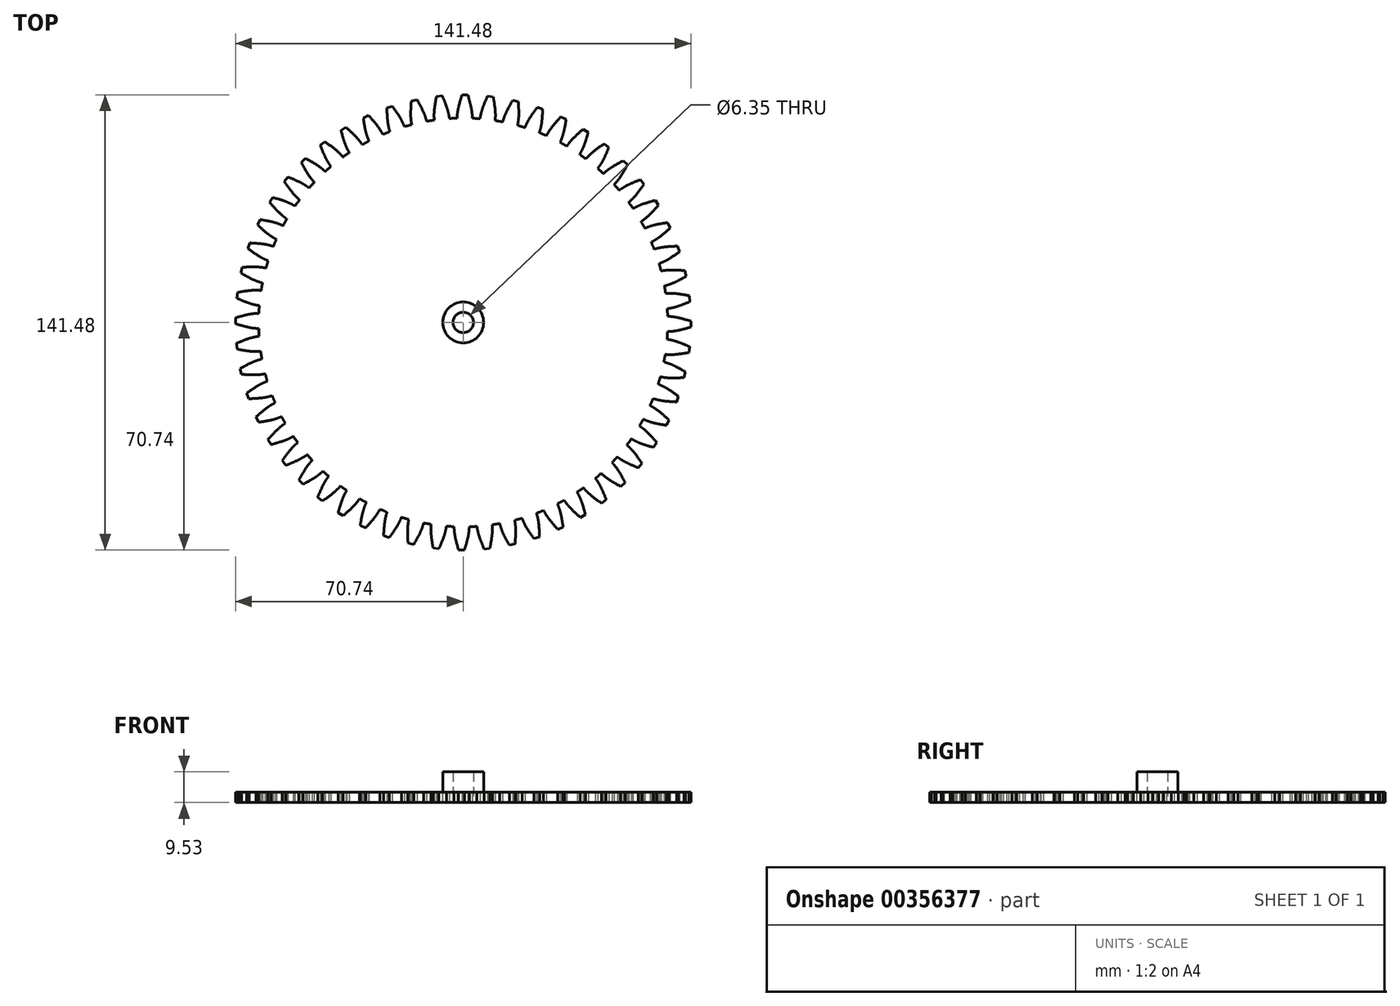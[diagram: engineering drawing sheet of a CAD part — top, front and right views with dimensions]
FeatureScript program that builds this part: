
annotation { "Feature Type Name" : "Feature", "Feature Type Description" : "" }
export const myFeature = defineFeature(function(context is Context, id is Id, definition is map)
    precondition{}
    {
        {
            var Q0;
            Q0=qCreatedBy(makeId("Top.planeOp"),FACE);
            var sketch = newSketch(context, id + "F0", { "sketchPlane" : qUnion([Q0])});
            skLineSegment(sketch, "E0.14", {"start": v(5.82, 65.97) * mm, "end": v(9.98, 65.46) * mm});
            skLineSegment(sketch, "E1.14", {"start": v(5.22, 63.33) * mm, "end": v(9.94, 62.76) * mm});
            skLineSegment(sketch, "E2", {"start": v(0, 0) * mm, "end": v(8.44, 70.23) * mm});
            skLineSegment(sketch, "E3", {"start": v(7.53, 70.34) * mm, "end": v(9.35, 70.12) * mm});
            skPoint(sketch, "E4", {"position": v(7.58, 63.05) * mm});
            skPoint(sketch, "E5", {"position": v(7.9, 65.72) * mm});
            skPoint(sketch, "E6", {"position": v(8.44, 70.23) * mm});
            skFitSpline(sketch, "E7", {"points": [v(5.22, 63.33) * mm, v(5.82, 65.97) * mm, v(7.53, 70.34) * mm], "startDerivative": vector(1.04, 5.77) * mm, "endDerivative": vector(3.48, 8.14) * mm});
            skFitSpline(sketch, "E8", {"points": [v(9.35, 70.12) * mm, v(9.98, 65.46) * mm, v(9.94, 62.76) * mm], "startDerivative": vector(1.45, -8.73) * mm, "endDerivative": vector(-0.36, -5.85) * mm});
            skCircle(sketch, "E9", {"center": v(0, 0) * mm, "radius": 63.54 * mm});
            skSolve(sketch);
        }
        {
            var Q0;
            Q0 = qSketchRegion(id + "F0", true);
            extrude(context, id + "F1", {"entities" : qUnion([Q0]), "depth" : 3.17 * mm, "offsetDistance" : 25.4 * mm});
        }
        {
            var Q0;
            Q0=qCreatedBy(makeId("Front.planeOp"),FACE);
            var sketch = newSketch(context, id + "F2", { "sketchPlane" : qUnion([Q0])});
            skLineSegment(sketch, "E10", {"start": v(0, 0) * mm, "end": v(0, 55.23) * mm});
            skSolve(sketch);
        }
        {
            var Q0;
            Q0=makeQuery(id+"F1.opExtrude","SWEPT_BODY",BODY,{"disambiguationData":[OSD([sQuery(id+"F0.wireOp",EDGE,"E3"),sQuery(id+"F0.wireOp",EDGE,"E7"),sQuery(id+"F0.wireOp",EDGE,"E8"),sQuery(id+"F0.wireOp",EDGE,"E9")])]});
            var Q1;
            Q1=sQuery(id+"F2.wireOp",EDGE,"E10");
            circularPattern(context, id + "F3", {"entities" : qUnion([Q0]), "axis" : qUnion([Q1]), "angle" : 360 * degree, "instanceCount" : 56, "equalSpace" : true});
        }
        {
            var Q0;
            Q0=makeQuery(id+"F3.opPattern","COPY",BODY,{"derivedFrom":makeQuery(id+"F1.opExtrude","SWEPT_BODY",BODY,{"disambiguationData":[OSD([sQuery(id+"F0.wireOp",EDGE,"E3"),sQuery(id+"F0.wireOp",EDGE,"E7"),sQuery(id+"F0.wireOp",EDGE,"E8"),sQuery(id+"F0.wireOp",EDGE,"E9")])]}),"instanceName":"55"});
            var Q1;
            Q1=makeQuery(id+"F3.opPattern","COPY",BODY,{"derivedFrom":makeQuery(id+"F1.opExtrude","SWEPT_BODY",BODY,{"disambiguationData":[OSD([sQuery(id+"F0.wireOp",EDGE,"E3"),sQuery(id+"F0.wireOp",EDGE,"E7"),sQuery(id+"F0.wireOp",EDGE,"E8"),sQuery(id+"F0.wireOp",EDGE,"E9")])]}),"instanceName":"6"});
            var Q2;
            Q2=makeQuery(id+"F3.opPattern","COPY",BODY,{"derivedFrom":makeQuery(id+"F1.opExtrude","SWEPT_BODY",BODY,{"disambiguationData":[OSD([sQuery(id+"F0.wireOp",EDGE,"E3"),sQuery(id+"F0.wireOp",EDGE,"E7"),sQuery(id+"F0.wireOp",EDGE,"E8"),sQuery(id+"F0.wireOp",EDGE,"E9")])]}),"instanceName":"11"});
            var Q3;
            Q3=makeQuery(id+"F3.opPattern","COPY",BODY,{"derivedFrom":makeQuery(id+"F1.opExtrude","SWEPT_BODY",BODY,{"disambiguationData":[OSD([sQuery(id+"F0.wireOp",EDGE,"E3"),sQuery(id+"F0.wireOp",EDGE,"E7"),sQuery(id+"F0.wireOp",EDGE,"E8"),sQuery(id+"F0.wireOp",EDGE,"E9")])]}),"instanceName":"30"});
            var Q4;
            Q4=makeQuery(id+"F3.opPattern","COPY",BODY,{"derivedFrom":makeQuery(id+"F1.opExtrude","SWEPT_BODY",BODY,{"disambiguationData":[OSD([sQuery(id+"F0.wireOp",EDGE,"E3"),sQuery(id+"F0.wireOp",EDGE,"E7"),sQuery(id+"F0.wireOp",EDGE,"E8"),sQuery(id+"F0.wireOp",EDGE,"E9")])]}),"instanceName":"24"});
            var Q5;
            Q5=makeQuery(id+"F3.opPattern","COPY",BODY,{"derivedFrom":makeQuery(id+"F1.opExtrude","SWEPT_BODY",BODY,{"disambiguationData":[OSD([sQuery(id+"F0.wireOp",EDGE,"E3"),sQuery(id+"F0.wireOp",EDGE,"E7"),sQuery(id+"F0.wireOp",EDGE,"E8"),sQuery(id+"F0.wireOp",EDGE,"E9")])]}),"instanceName":"44"});
            var Q6;
            Q6=makeQuery(id+"F3.opPattern","COPY",BODY,{"derivedFrom":makeQuery(id+"F1.opExtrude","SWEPT_BODY",BODY,{"disambiguationData":[OSD([sQuery(id+"F0.wireOp",EDGE,"E3"),sQuery(id+"F0.wireOp",EDGE,"E7"),sQuery(id+"F0.wireOp",EDGE,"E8"),sQuery(id+"F0.wireOp",EDGE,"E9")])]}),"instanceName":"8"});
            var Q7;
            Q7=makeQuery(id+"F3.opPattern","COPY",BODY,{"derivedFrom":makeQuery(id+"F1.opExtrude","SWEPT_BODY",BODY,{"disambiguationData":[OSD([sQuery(id+"F0.wireOp",EDGE,"E3"),sQuery(id+"F0.wireOp",EDGE,"E7"),sQuery(id+"F0.wireOp",EDGE,"E8"),sQuery(id+"F0.wireOp",EDGE,"E9")])]}),"instanceName":"39"});
            var Q8;
            Q8=makeQuery(id+"F3.opPattern","COPY",BODY,{"derivedFrom":makeQuery(id+"F1.opExtrude","SWEPT_BODY",BODY,{"disambiguationData":[OSD([sQuery(id+"F0.wireOp",EDGE,"E3"),sQuery(id+"F0.wireOp",EDGE,"E7"),sQuery(id+"F0.wireOp",EDGE,"E8"),sQuery(id+"F0.wireOp",EDGE,"E9")])]}),"instanceName":"42"});
            var Q9;
            Q9=makeQuery(id+"F3.opPattern","COPY",BODY,{"derivedFrom":makeQuery(id+"F1.opExtrude","SWEPT_BODY",BODY,{"disambiguationData":[OSD([sQuery(id+"F0.wireOp",EDGE,"E3"),sQuery(id+"F0.wireOp",EDGE,"E7"),sQuery(id+"F0.wireOp",EDGE,"E8"),sQuery(id+"F0.wireOp",EDGE,"E9")])]}),"instanceName":"5"});
            var Q10;
            Q10=makeQuery(id+"F3.opPattern","COPY",BODY,{"derivedFrom":makeQuery(id+"F1.opExtrude","SWEPT_BODY",BODY,{"disambiguationData":[OSD([sQuery(id+"F0.wireOp",EDGE,"E3"),sQuery(id+"F0.wireOp",EDGE,"E7"),sQuery(id+"F0.wireOp",EDGE,"E8"),sQuery(id+"F0.wireOp",EDGE,"E9")])]}),"instanceName":"26"});
            var Q11;
            Q11=makeQuery(id+"F3.opPattern","COPY",BODY,{"derivedFrom":makeQuery(id+"F1.opExtrude","SWEPT_BODY",BODY,{"disambiguationData":[OSD([sQuery(id+"F0.wireOp",EDGE,"E3"),sQuery(id+"F0.wireOp",EDGE,"E7"),sQuery(id+"F0.wireOp",EDGE,"E8"),sQuery(id+"F0.wireOp",EDGE,"E9")])]}),"instanceName":"41"});
            var Q12;
            Q12=makeQuery(id+"F3.opPattern","COPY",BODY,{"derivedFrom":makeQuery(id+"F1.opExtrude","SWEPT_BODY",BODY,{"disambiguationData":[OSD([sQuery(id+"F0.wireOp",EDGE,"E3"),sQuery(id+"F0.wireOp",EDGE,"E7"),sQuery(id+"F0.wireOp",EDGE,"E8"),sQuery(id+"F0.wireOp",EDGE,"E9")])]}),"instanceName":"20"});
            var Q13;
            Q13=makeQuery(id+"F3.opPattern","COPY",BODY,{"derivedFrom":makeQuery(id+"F1.opExtrude","SWEPT_BODY",BODY,{"disambiguationData":[OSD([sQuery(id+"F0.wireOp",EDGE,"E3"),sQuery(id+"F0.wireOp",EDGE,"E7"),sQuery(id+"F0.wireOp",EDGE,"E8"),sQuery(id+"F0.wireOp",EDGE,"E9")])]}),"instanceName":"59"});
            var Q14;
            Q14=makeQuery(id+"F3.opPattern","COPY",BODY,{"derivedFrom":makeQuery(id+"F1.opExtrude","SWEPT_BODY",BODY,{"disambiguationData":[OSD([sQuery(id+"F0.wireOp",EDGE,"E3"),sQuery(id+"F0.wireOp",EDGE,"E7"),sQuery(id+"F0.wireOp",EDGE,"E8"),sQuery(id+"F0.wireOp",EDGE,"E9")])]}),"instanceName":"29"});
            var Q15;
            Q15=makeQuery(id+"F3.opPattern","COPY",BODY,{"derivedFrom":makeQuery(id+"F1.opExtrude","SWEPT_BODY",BODY,{"disambiguationData":[OSD([sQuery(id+"F0.wireOp",EDGE,"E3"),sQuery(id+"F0.wireOp",EDGE,"E7"),sQuery(id+"F0.wireOp",EDGE,"E8"),sQuery(id+"F0.wireOp",EDGE,"E9")])]}),"instanceName":"35"});
            var Q16;
            Q16=makeQuery(id+"F3.opPattern","COPY",BODY,{"derivedFrom":makeQuery(id+"F1.opExtrude","SWEPT_BODY",BODY,{"disambiguationData":[OSD([sQuery(id+"F0.wireOp",EDGE,"E3"),sQuery(id+"F0.wireOp",EDGE,"E7"),sQuery(id+"F0.wireOp",EDGE,"E8"),sQuery(id+"F0.wireOp",EDGE,"E9")])]}),"instanceName":"54"});
            var Q17;
            Q17=makeQuery(id+"F3.opPattern","COPY",BODY,{"derivedFrom":makeQuery(id+"F1.opExtrude","SWEPT_BODY",BODY,{"disambiguationData":[OSD([sQuery(id+"F0.wireOp",EDGE,"E3"),sQuery(id+"F0.wireOp",EDGE,"E7"),sQuery(id+"F0.wireOp",EDGE,"E8"),sQuery(id+"F0.wireOp",EDGE,"E9")])]}),"instanceName":"48"});
            var Q18;
            Q18=makeQuery(id+"F3.opPattern","COPY",BODY,{"derivedFrom":makeQuery(id+"F1.opExtrude","SWEPT_BODY",BODY,{"disambiguationData":[OSD([sQuery(id+"F0.wireOp",EDGE,"E3"),sQuery(id+"F0.wireOp",EDGE,"E7"),sQuery(id+"F0.wireOp",EDGE,"E8"),sQuery(id+"F0.wireOp",EDGE,"E9")])]}),"instanceName":"14"});
            var Q19;
            Q19=makeQuery(id+"F3.opPattern","COPY",BODY,{"derivedFrom":makeQuery(id+"F1.opExtrude","SWEPT_BODY",BODY,{"disambiguationData":[OSD([sQuery(id+"F0.wireOp",EDGE,"E3"),sQuery(id+"F0.wireOp",EDGE,"E7"),sQuery(id+"F0.wireOp",EDGE,"E8"),sQuery(id+"F0.wireOp",EDGE,"E9")])]}),"instanceName":"56"});
            var Q20;
            Q20=makeQuery(id+"F3.opPattern","COPY",BODY,{"derivedFrom":makeQuery(id+"F1.opExtrude","SWEPT_BODY",BODY,{"disambiguationData":[OSD([sQuery(id+"F0.wireOp",EDGE,"E3"),sQuery(id+"F0.wireOp",EDGE,"E7"),sQuery(id+"F0.wireOp",EDGE,"E8"),sQuery(id+"F0.wireOp",EDGE,"E9")])]}),"instanceName":"12"});
            var Q21;
            Q21=makeQuery(id+"F1.opExtrude","SWEPT_BODY",BODY,{"disambiguationData":[OSD([sQuery(id+"F0.wireOp",EDGE,"E3"),sQuery(id+"F0.wireOp",EDGE,"E7"),sQuery(id+"F0.wireOp",EDGE,"E8"),sQuery(id+"F0.wireOp",EDGE,"E9")])]});
            var Q22;
            Q22=makeQuery(id+"F3.opPattern","COPY",BODY,{"derivedFrom":makeQuery(id+"F1.opExtrude","SWEPT_BODY",BODY,{"disambiguationData":[OSD([sQuery(id+"F0.wireOp",EDGE,"E3"),sQuery(id+"F0.wireOp",EDGE,"E7"),sQuery(id+"F0.wireOp",EDGE,"E8"),sQuery(id+"F0.wireOp",EDGE,"E9")])]}),"instanceName":"49"});
            var Q23;
            Q23=makeQuery(id+"F3.opPattern","COPY",BODY,{"derivedFrom":makeQuery(id+"F1.opExtrude","SWEPT_BODY",BODY,{"disambiguationData":[OSD([sQuery(id+"F0.wireOp",EDGE,"E3"),sQuery(id+"F0.wireOp",EDGE,"E7"),sQuery(id+"F0.wireOp",EDGE,"E8"),sQuery(id+"F0.wireOp",EDGE,"E9")])]}),"instanceName":"37"});
            var Q24;
            Q24=makeQuery(id+"F3.opPattern","COPY",BODY,{"derivedFrom":makeQuery(id+"F1.opExtrude","SWEPT_BODY",BODY,{"disambiguationData":[OSD([sQuery(id+"F0.wireOp",EDGE,"E3"),sQuery(id+"F0.wireOp",EDGE,"E7"),sQuery(id+"F0.wireOp",EDGE,"E8"),sQuery(id+"F0.wireOp",EDGE,"E9")])]}),"instanceName":"34"});
            var Q25;
            Q25=makeQuery(id+"F3.opPattern","COPY",BODY,{"derivedFrom":makeQuery(id+"F1.opExtrude","SWEPT_BODY",BODY,{"disambiguationData":[OSD([sQuery(id+"F0.wireOp",EDGE,"E3"),sQuery(id+"F0.wireOp",EDGE,"E7"),sQuery(id+"F0.wireOp",EDGE,"E8"),sQuery(id+"F0.wireOp",EDGE,"E9")])]}),"instanceName":"52"});
            var Q26;
            Q26=makeQuery(id+"F3.opPattern","COPY",BODY,{"derivedFrom":makeQuery(id+"F1.opExtrude","SWEPT_BODY",BODY,{"disambiguationData":[OSD([sQuery(id+"F0.wireOp",EDGE,"E3"),sQuery(id+"F0.wireOp",EDGE,"E7"),sQuery(id+"F0.wireOp",EDGE,"E8"),sQuery(id+"F0.wireOp",EDGE,"E9")])]}),"instanceName":"1"});
            var Q27;
            Q27=makeQuery(id+"F3.opPattern","COPY",BODY,{"derivedFrom":makeQuery(id+"F1.opExtrude","SWEPT_BODY",BODY,{"disambiguationData":[OSD([sQuery(id+"F0.wireOp",EDGE,"E3"),sQuery(id+"F0.wireOp",EDGE,"E7"),sQuery(id+"F0.wireOp",EDGE,"E8"),sQuery(id+"F0.wireOp",EDGE,"E9")])]}),"instanceName":"21"});
            var Q28;
            Q28=makeQuery(id+"F3.opPattern","COPY",BODY,{"derivedFrom":makeQuery(id+"F1.opExtrude","SWEPT_BODY",BODY,{"disambiguationData":[OSD([sQuery(id+"F0.wireOp",EDGE,"E3"),sQuery(id+"F0.wireOp",EDGE,"E7"),sQuery(id+"F0.wireOp",EDGE,"E8"),sQuery(id+"F0.wireOp",EDGE,"E9")])]}),"instanceName":"33"});
            var Q29;
            Q29=makeQuery(id+"F3.opPattern","COPY",BODY,{"derivedFrom":makeQuery(id+"F1.opExtrude","SWEPT_BODY",BODY,{"disambiguationData":[OSD([sQuery(id+"F0.wireOp",EDGE,"E3"),sQuery(id+"F0.wireOp",EDGE,"E7"),sQuery(id+"F0.wireOp",EDGE,"E8"),sQuery(id+"F0.wireOp",EDGE,"E9")])]}),"instanceName":"25"});
            var Q30;
            Q30=makeQuery(id+"F3.opPattern","COPY",BODY,{"derivedFrom":makeQuery(id+"F1.opExtrude","SWEPT_BODY",BODY,{"disambiguationData":[OSD([sQuery(id+"F0.wireOp",EDGE,"E3"),sQuery(id+"F0.wireOp",EDGE,"E7"),sQuery(id+"F0.wireOp",EDGE,"E8"),sQuery(id+"F0.wireOp",EDGE,"E9")])]}),"instanceName":"57"});
            var Q31;
            Q31=makeQuery(id+"F3.opPattern","COPY",BODY,{"derivedFrom":makeQuery(id+"F1.opExtrude","SWEPT_BODY",BODY,{"disambiguationData":[OSD([sQuery(id+"F0.wireOp",EDGE,"E3"),sQuery(id+"F0.wireOp",EDGE,"E7"),sQuery(id+"F0.wireOp",EDGE,"E8"),sQuery(id+"F0.wireOp",EDGE,"E9")])]}),"instanceName":"2"});
            var Q32;
            Q32=makeQuery(id+"F3.opPattern","COPY",BODY,{"derivedFrom":makeQuery(id+"F1.opExtrude","SWEPT_BODY",BODY,{"disambiguationData":[OSD([sQuery(id+"F0.wireOp",EDGE,"E3"),sQuery(id+"F0.wireOp",EDGE,"E7"),sQuery(id+"F0.wireOp",EDGE,"E8"),sQuery(id+"F0.wireOp",EDGE,"E9")])]}),"instanceName":"53"});
            var Q33;
            Q33=makeQuery(id+"F3.opPattern","COPY",BODY,{"derivedFrom":makeQuery(id+"F1.opExtrude","SWEPT_BODY",BODY,{"disambiguationData":[OSD([sQuery(id+"F0.wireOp",EDGE,"E3"),sQuery(id+"F0.wireOp",EDGE,"E7"),sQuery(id+"F0.wireOp",EDGE,"E8"),sQuery(id+"F0.wireOp",EDGE,"E9")])]}),"instanceName":"13"});
            var Q34;
            Q34=makeQuery(id+"F3.opPattern","COPY",BODY,{"derivedFrom":makeQuery(id+"F1.opExtrude","SWEPT_BODY",BODY,{"disambiguationData":[OSD([sQuery(id+"F0.wireOp",EDGE,"E3"),sQuery(id+"F0.wireOp",EDGE,"E7"),sQuery(id+"F0.wireOp",EDGE,"E8"),sQuery(id+"F0.wireOp",EDGE,"E9")])]}),"instanceName":"16"});
            var Q35;
            Q35=makeQuery(id+"F3.opPattern","COPY",BODY,{"derivedFrom":makeQuery(id+"F1.opExtrude","SWEPT_BODY",BODY,{"disambiguationData":[OSD([sQuery(id+"F0.wireOp",EDGE,"E3"),sQuery(id+"F0.wireOp",EDGE,"E7"),sQuery(id+"F0.wireOp",EDGE,"E8"),sQuery(id+"F0.wireOp",EDGE,"E9")])]}),"instanceName":"50"});
            var Q36;
            Q36=makeQuery(id+"F3.opPattern","COPY",BODY,{"derivedFrom":makeQuery(id+"F1.opExtrude","SWEPT_BODY",BODY,{"disambiguationData":[OSD([sQuery(id+"F0.wireOp",EDGE,"E3"),sQuery(id+"F0.wireOp",EDGE,"E7"),sQuery(id+"F0.wireOp",EDGE,"E8"),sQuery(id+"F0.wireOp",EDGE,"E9")])]}),"instanceName":"22"});
            var Q37;
            Q37=makeQuery(id+"F3.opPattern","COPY",BODY,{"derivedFrom":makeQuery(id+"F1.opExtrude","SWEPT_BODY",BODY,{"disambiguationData":[OSD([sQuery(id+"F0.wireOp",EDGE,"E3"),sQuery(id+"F0.wireOp",EDGE,"E7"),sQuery(id+"F0.wireOp",EDGE,"E8"),sQuery(id+"F0.wireOp",EDGE,"E9")])]}),"instanceName":"31"});
            var Q38;
            Q38=makeQuery(id+"F3.opPattern","COPY",BODY,{"derivedFrom":makeQuery(id+"F1.opExtrude","SWEPT_BODY",BODY,{"disambiguationData":[OSD([sQuery(id+"F0.wireOp",EDGE,"E3"),sQuery(id+"F0.wireOp",EDGE,"E7"),sQuery(id+"F0.wireOp",EDGE,"E8"),sQuery(id+"F0.wireOp",EDGE,"E9")])]}),"instanceName":"36"});
            var Q39;
            Q39=makeQuery(id+"F3.opPattern","COPY",BODY,{"derivedFrom":makeQuery(id+"F1.opExtrude","SWEPT_BODY",BODY,{"disambiguationData":[OSD([sQuery(id+"F0.wireOp",EDGE,"E3"),sQuery(id+"F0.wireOp",EDGE,"E7"),sQuery(id+"F0.wireOp",EDGE,"E8"),sQuery(id+"F0.wireOp",EDGE,"E9")])]}),"instanceName":"46"});
            var Q40;
            Q40=makeQuery(id+"F3.opPattern","COPY",BODY,{"derivedFrom":makeQuery(id+"F1.opExtrude","SWEPT_BODY",BODY,{"disambiguationData":[OSD([sQuery(id+"F0.wireOp",EDGE,"E3"),sQuery(id+"F0.wireOp",EDGE,"E7"),sQuery(id+"F0.wireOp",EDGE,"E8"),sQuery(id+"F0.wireOp",EDGE,"E9")])]}),"instanceName":"32"});
            var Q41;
            Q41=makeQuery(id+"F3.opPattern","COPY",BODY,{"derivedFrom":makeQuery(id+"F1.opExtrude","SWEPT_BODY",BODY,{"disambiguationData":[OSD([sQuery(id+"F0.wireOp",EDGE,"E3"),sQuery(id+"F0.wireOp",EDGE,"E7"),sQuery(id+"F0.wireOp",EDGE,"E8"),sQuery(id+"F0.wireOp",EDGE,"E9")])]}),"instanceName":"15"});
            var Q42;
            Q42=makeQuery(id+"F3.opPattern","COPY",BODY,{"derivedFrom":makeQuery(id+"F1.opExtrude","SWEPT_BODY",BODY,{"disambiguationData":[OSD([sQuery(id+"F0.wireOp",EDGE,"E3"),sQuery(id+"F0.wireOp",EDGE,"E7"),sQuery(id+"F0.wireOp",EDGE,"E8"),sQuery(id+"F0.wireOp",EDGE,"E9")])]}),"instanceName":"9"});
            var Q43;
            Q43=makeQuery(id+"F3.opPattern","COPY",BODY,{"derivedFrom":makeQuery(id+"F1.opExtrude","SWEPT_BODY",BODY,{"disambiguationData":[OSD([sQuery(id+"F0.wireOp",EDGE,"E3"),sQuery(id+"F0.wireOp",EDGE,"E7"),sQuery(id+"F0.wireOp",EDGE,"E8"),sQuery(id+"F0.wireOp",EDGE,"E9")])]}),"instanceName":"28"});
            var Q44;
            Q44=makeQuery(id+"F3.opPattern","COPY",BODY,{"derivedFrom":makeQuery(id+"F1.opExtrude","SWEPT_BODY",BODY,{"disambiguationData":[OSD([sQuery(id+"F0.wireOp",EDGE,"E3"),sQuery(id+"F0.wireOp",EDGE,"E7"),sQuery(id+"F0.wireOp",EDGE,"E8"),sQuery(id+"F0.wireOp",EDGE,"E9")])]}),"instanceName":"43"});
            var Q45;
            Q45=makeQuery(id+"F3.opPattern","COPY",BODY,{"derivedFrom":makeQuery(id+"F1.opExtrude","SWEPT_BODY",BODY,{"disambiguationData":[OSD([sQuery(id+"F0.wireOp",EDGE,"E3"),sQuery(id+"F0.wireOp",EDGE,"E7"),sQuery(id+"F0.wireOp",EDGE,"E8"),sQuery(id+"F0.wireOp",EDGE,"E9")])]}),"instanceName":"51"});
            var Q46;
            Q46=makeQuery(id+"F3.opPattern","COPY",BODY,{"derivedFrom":makeQuery(id+"F1.opExtrude","SWEPT_BODY",BODY,{"disambiguationData":[OSD([sQuery(id+"F0.wireOp",EDGE,"E3"),sQuery(id+"F0.wireOp",EDGE,"E7"),sQuery(id+"F0.wireOp",EDGE,"E8"),sQuery(id+"F0.wireOp",EDGE,"E9")])]}),"instanceName":"45"});
            var Q47;
            Q47=makeQuery(id+"F3.opPattern","COPY",BODY,{"derivedFrom":makeQuery(id+"F1.opExtrude","SWEPT_BODY",BODY,{"disambiguationData":[OSD([sQuery(id+"F0.wireOp",EDGE,"E3"),sQuery(id+"F0.wireOp",EDGE,"E7"),sQuery(id+"F0.wireOp",EDGE,"E8"),sQuery(id+"F0.wireOp",EDGE,"E9")])]}),"instanceName":"7"});
            var Q48;
            Q48=makeQuery(id+"F3.opPattern","COPY",BODY,{"derivedFrom":makeQuery(id+"F1.opExtrude","SWEPT_BODY",BODY,{"disambiguationData":[OSD([sQuery(id+"F0.wireOp",EDGE,"E3"),sQuery(id+"F0.wireOp",EDGE,"E7"),sQuery(id+"F0.wireOp",EDGE,"E8"),sQuery(id+"F0.wireOp",EDGE,"E9")])]}),"instanceName":"40"});
            var Q49;
            Q49=makeQuery(id+"F3.opPattern","COPY",BODY,{"derivedFrom":makeQuery(id+"F1.opExtrude","SWEPT_BODY",BODY,{"disambiguationData":[OSD([sQuery(id+"F0.wireOp",EDGE,"E3"),sQuery(id+"F0.wireOp",EDGE,"E7"),sQuery(id+"F0.wireOp",EDGE,"E8"),sQuery(id+"F0.wireOp",EDGE,"E9")])]}),"instanceName":"3"});
            var Q50;
            Q50=makeQuery(id+"F3.opPattern","COPY",BODY,{"derivedFrom":makeQuery(id+"F1.opExtrude","SWEPT_BODY",BODY,{"disambiguationData":[OSD([sQuery(id+"F0.wireOp",EDGE,"E3"),sQuery(id+"F0.wireOp",EDGE,"E7"),sQuery(id+"F0.wireOp",EDGE,"E8"),sQuery(id+"F0.wireOp",EDGE,"E9")])]}),"instanceName":"23"});
            var Q51;
            Q51=makeQuery(id+"F3.opPattern","COPY",BODY,{"derivedFrom":makeQuery(id+"F1.opExtrude","SWEPT_BODY",BODY,{"disambiguationData":[OSD([sQuery(id+"F0.wireOp",EDGE,"E3"),sQuery(id+"F0.wireOp",EDGE,"E7"),sQuery(id+"F0.wireOp",EDGE,"E8"),sQuery(id+"F0.wireOp",EDGE,"E9")])]}),"instanceName":"58"});
            var Q52;
            Q52=makeQuery(id+"F3.opPattern","COPY",BODY,{"derivedFrom":makeQuery(id+"F1.opExtrude","SWEPT_BODY",BODY,{"disambiguationData":[OSD([sQuery(id+"F0.wireOp",EDGE,"E3"),sQuery(id+"F0.wireOp",EDGE,"E7"),sQuery(id+"F0.wireOp",EDGE,"E8"),sQuery(id+"F0.wireOp",EDGE,"E9")])]}),"instanceName":"47"});
            var Q53;
            Q53=makeQuery(id+"F3.opPattern","COPY",BODY,{"derivedFrom":makeQuery(id+"F1.opExtrude","SWEPT_BODY",BODY,{"disambiguationData":[OSD([sQuery(id+"F0.wireOp",EDGE,"E3"),sQuery(id+"F0.wireOp",EDGE,"E7"),sQuery(id+"F0.wireOp",EDGE,"E8"),sQuery(id+"F0.wireOp",EDGE,"E9")])]}),"instanceName":"38"});
            var Q54;
            Q54=makeQuery(id+"F3.opPattern","COPY",BODY,{"derivedFrom":makeQuery(id+"F1.opExtrude","SWEPT_BODY",BODY,{"disambiguationData":[OSD([sQuery(id+"F0.wireOp",EDGE,"E3"),sQuery(id+"F0.wireOp",EDGE,"E7"),sQuery(id+"F0.wireOp",EDGE,"E8"),sQuery(id+"F0.wireOp",EDGE,"E9")])]}),"instanceName":"10"});
            var Q55;
            Q55=makeQuery(id+"F3.opPattern","COPY",BODY,{"derivedFrom":makeQuery(id+"F1.opExtrude","SWEPT_BODY",BODY,{"disambiguationData":[OSD([sQuery(id+"F0.wireOp",EDGE,"E3"),sQuery(id+"F0.wireOp",EDGE,"E7"),sQuery(id+"F0.wireOp",EDGE,"E8"),sQuery(id+"F0.wireOp",EDGE,"E9")])]}),"instanceName":"17"});
            var Q56;
            Q56=makeQuery(id+"F3.opPattern","COPY",BODY,{"derivedFrom":makeQuery(id+"F1.opExtrude","SWEPT_BODY",BODY,{"disambiguationData":[OSD([sQuery(id+"F0.wireOp",EDGE,"E3"),sQuery(id+"F0.wireOp",EDGE,"E7"),sQuery(id+"F0.wireOp",EDGE,"E8"),sQuery(id+"F0.wireOp",EDGE,"E9")])]}),"instanceName":"18"});
            var Q57;
            Q57=makeQuery(id+"F3.opPattern","COPY",BODY,{"derivedFrom":makeQuery(id+"F1.opExtrude","SWEPT_BODY",BODY,{"disambiguationData":[OSD([sQuery(id+"F0.wireOp",EDGE,"E3"),sQuery(id+"F0.wireOp",EDGE,"E7"),sQuery(id+"F0.wireOp",EDGE,"E8"),sQuery(id+"F0.wireOp",EDGE,"E9")])]}),"instanceName":"19"});
            var Q58;
            Q58=makeQuery(id+"F3.opPattern","COPY",BODY,{"derivedFrom":makeQuery(id+"F1.opExtrude","SWEPT_BODY",BODY,{"disambiguationData":[OSD([sQuery(id+"F0.wireOp",EDGE,"E3"),sQuery(id+"F0.wireOp",EDGE,"E7"),sQuery(id+"F0.wireOp",EDGE,"E8"),sQuery(id+"F0.wireOp",EDGE,"E9")])]}),"instanceName":"27"});
            var Q59;
            Q59=makeQuery(id+"F3.opPattern","COPY",BODY,{"derivedFrom":makeQuery(id+"F1.opExtrude","SWEPT_BODY",BODY,{"disambiguationData":[OSD([sQuery(id+"F0.wireOp",EDGE,"E3"),sQuery(id+"F0.wireOp",EDGE,"E7"),sQuery(id+"F0.wireOp",EDGE,"E8"),sQuery(id+"F0.wireOp",EDGE,"E9")])]}),"instanceName":"4"});
            booleanBodies(context, id + "F4", {"operationType" : BooleanOperationType.UNION, "tools" : qUnion([Q0, Q1, Q2, Q3, Q4, Q5, Q6, Q7, Q8, Q9, Q10, Q11, Q12, Q13, Q14, Q15, Q16, Q17, Q18, Q19, Q20, Q21, Q22, Q23, Q24, Q25, Q26, Q27, Q28, Q29, Q30, Q31, Q32, Q33, Q34, Q35, Q36, Q37, Q38, Q39, Q40, Q41, Q42, Q43, Q44, Q45, Q46, Q47, Q48, Q49, Q50, Q51, Q52, Q53, Q54, Q55, Q56, Q57, Q58, Q59])});
        }
        {
            var Q0;
            {var subQ0=makeQuery(id+"F1.opExtrude","CAP_FACE",FACE,{"disambiguationData":[OSD([sQuery(id+"F0.wireOp",EDGE,"E3"),sQuery(id+"F0.wireOp",EDGE,"E7"),sQuery(id+"F0.wireOp",EDGE,"E8"),sQuery(id+"F0.wireOp",EDGE,"E9")])],"isStart":false});Q0=makeQuery(id+"F4.opBoolean","MERGE",FACE,{"derivedFrom":[subQ0,makeQuery(id+"F3.opPattern","COPY",FACE,{"derivedFrom":subQ0,"instanceName":"1"}),makeQuery(id+"F3.opPattern","COPY",FACE,{"derivedFrom":subQ0,"instanceName":"2"}),makeQuery(id+"F3.opPattern","COPY",FACE,{"derivedFrom":subQ0,"instanceName":"3"}),makeQuery(id+"F3.opPattern","COPY",FACE,{"derivedFrom":subQ0,"instanceName":"4"}),makeQuery(id+"F3.opPattern","COPY",FACE,{"derivedFrom":subQ0,"instanceName":"5"}),makeQuery(id+"F3.opPattern","COPY",FACE,{"derivedFrom":subQ0,"instanceName":"6"}),makeQuery(id+"F3.opPattern","COPY",FACE,{"derivedFrom":subQ0,"instanceName":"7"}),makeQuery(id+"F3.opPattern","COPY",FACE,{"derivedFrom":subQ0,"instanceName":"8"}),makeQuery(id+"F3.opPattern","COPY",FACE,{"derivedFrom":subQ0,"instanceName":"9"}),makeQuery(id+"F3.opPattern","COPY",FACE,{"derivedFrom":subQ0,"instanceName":"10"}),makeQuery(id+"F3.opPattern","COPY",FACE,{"derivedFrom":subQ0,"instanceName":"11"}),makeQuery(id+"F3.opPattern","COPY",FACE,{"derivedFrom":subQ0,"instanceName":"12"}),makeQuery(id+"F3.opPattern","COPY",FACE,{"derivedFrom":subQ0,"instanceName":"13"}),makeQuery(id+"F3.opPattern","COPY",FACE,{"derivedFrom":subQ0,"instanceName":"14"}),makeQuery(id+"F3.opPattern","COPY",FACE,{"derivedFrom":subQ0,"instanceName":"15"}),makeQuery(id+"F3.opPattern","COPY",FACE,{"derivedFrom":subQ0,"instanceName":"16"}),makeQuery(id+"F3.opPattern","COPY",FACE,{"derivedFrom":subQ0,"instanceName":"17"}),makeQuery(id+"F3.opPattern","COPY",FACE,{"derivedFrom":subQ0,"instanceName":"18"}),makeQuery(id+"F3.opPattern","COPY",FACE,{"derivedFrom":subQ0,"instanceName":"19"}),makeQuery(id+"F3.opPattern","COPY",FACE,{"derivedFrom":subQ0,"instanceName":"20"}),makeQuery(id+"F3.opPattern","COPY",FACE,{"derivedFrom":subQ0,"instanceName":"21"}),makeQuery(id+"F3.opPattern","COPY",FACE,{"derivedFrom":subQ0,"instanceName":"22"}),makeQuery(id+"F3.opPattern","COPY",FACE,{"derivedFrom":subQ0,"instanceName":"23"}),makeQuery(id+"F3.opPattern","COPY",FACE,{"derivedFrom":subQ0,"instanceName":"24"}),makeQuery(id+"F3.opPattern","COPY",FACE,{"derivedFrom":subQ0,"instanceName":"25"}),makeQuery(id+"F3.opPattern","COPY",FACE,{"derivedFrom":subQ0,"instanceName":"26"}),makeQuery(id+"F3.opPattern","COPY",FACE,{"derivedFrom":subQ0,"instanceName":"27"}),makeQuery(id+"F3.opPattern","COPY",FACE,{"derivedFrom":subQ0,"instanceName":"28"}),makeQuery(id+"F3.opPattern","COPY",FACE,{"derivedFrom":subQ0,"instanceName":"29"}),makeQuery(id+"F3.opPattern","COPY",FACE,{"derivedFrom":subQ0,"instanceName":"30"}),makeQuery(id+"F3.opPattern","COPY",FACE,{"derivedFrom":subQ0,"instanceName":"31"}),makeQuery(id+"F3.opPattern","COPY",FACE,{"derivedFrom":subQ0,"instanceName":"32"}),makeQuery(id+"F3.opPattern","COPY",FACE,{"derivedFrom":subQ0,"instanceName":"33"}),makeQuery(id+"F3.opPattern","COPY",FACE,{"derivedFrom":subQ0,"instanceName":"34"}),makeQuery(id+"F3.opPattern","COPY",FACE,{"derivedFrom":subQ0,"instanceName":"35"}),makeQuery(id+"F3.opPattern","COPY",FACE,{"derivedFrom":subQ0,"instanceName":"36"}),makeQuery(id+"F3.opPattern","COPY",FACE,{"derivedFrom":subQ0,"instanceName":"37"}),makeQuery(id+"F3.opPattern","COPY",FACE,{"derivedFrom":subQ0,"instanceName":"38"}),makeQuery(id+"F3.opPattern","COPY",FACE,{"derivedFrom":subQ0,"instanceName":"39"}),makeQuery(id+"F3.opPattern","COPY",FACE,{"derivedFrom":subQ0,"instanceName":"40"}),makeQuery(id+"F3.opPattern","COPY",FACE,{"derivedFrom":subQ0,"instanceName":"41"}),makeQuery(id+"F3.opPattern","COPY",FACE,{"derivedFrom":subQ0,"instanceName":"42"}),makeQuery(id+"F3.opPattern","COPY",FACE,{"derivedFrom":subQ0,"instanceName":"43"}),makeQuery(id+"F3.opPattern","COPY",FACE,{"derivedFrom":subQ0,"instanceName":"44"}),makeQuery(id+"F3.opPattern","COPY",FACE,{"derivedFrom":subQ0,"instanceName":"45"}),makeQuery(id+"F3.opPattern","COPY",FACE,{"derivedFrom":subQ0,"instanceName":"46"}),makeQuery(id+"F3.opPattern","COPY",FACE,{"derivedFrom":subQ0,"instanceName":"47"}),makeQuery(id+"F3.opPattern","COPY",FACE,{"derivedFrom":subQ0,"instanceName":"48"}),makeQuery(id+"F3.opPattern","COPY",FACE,{"derivedFrom":subQ0,"instanceName":"49"}),makeQuery(id+"F3.opPattern","COPY",FACE,{"derivedFrom":subQ0,"instanceName":"50"}),makeQuery(id+"F3.opPattern","COPY",FACE,{"derivedFrom":subQ0,"instanceName":"51"}),makeQuery(id+"F3.opPattern","COPY",FACE,{"derivedFrom":subQ0,"instanceName":"52"}),makeQuery(id+"F3.opPattern","COPY",FACE,{"derivedFrom":subQ0,"instanceName":"53"}),makeQuery(id+"F3.opPattern","COPY",FACE,{"derivedFrom":subQ0,"instanceName":"54"}),makeQuery(id+"F3.opPattern","COPY",FACE,{"derivedFrom":subQ0,"instanceName":"55"}),makeQuery(id+"F3.opPattern","COPY",FACE,{"derivedFrom":subQ0,"instanceName":"56"}),makeQuery(id+"F3.opPattern","COPY",FACE,{"derivedFrom":subQ0,"instanceName":"57"}),makeQuery(id+"F3.opPattern","COPY",FACE,{"derivedFrom":subQ0,"instanceName":"58"}),makeQuery(id+"F3.opPattern","COPY",FACE,{"derivedFrom":subQ0,"instanceName":"59"})]});}
            var sketch = newSketch(context, id + "F5", { "sketchPlane" : qUnion([Q0])});
            skCircle(sketch, "E11", {"center": v(0, 0) * mm, "radius": 3.18 * mm});
            skCircle(sketch, "E12", {"center": v(0, 0) * mm, "radius": 6.35 * mm});
            skSolve(sketch);
        }
        {
            var Q0;
            Q0=makeQuery(id+"F5.imprint","IMPRINT",FACE,{"disambiguationData":[TD([[makeQuery(id+"F5.imprint","IMPRINT",EDGE,{"derivedFrom":sQuery(id+"F5.wireOp",EDGE,"E11")}),-1.0]])]});
            extrude(context, id + "F6", {"entities" : qUnion([Q0]), "operationType" : NewBodyOperationType.ADD, "depth" : 6.35 * mm, "offsetDistance" : 25.4 * mm});
        }
        {
            var Q0;
            {var subQ0=makeQuery(id+"F1.opExtrude","CAP_FACE",FACE,{"disambiguationData":[OSD([sQuery(id+"F0.wireOp",EDGE,"E3"),sQuery(id+"F0.wireOp",EDGE,"E7"),sQuery(id+"F0.wireOp",EDGE,"E8"),sQuery(id+"F0.wireOp",EDGE,"E9")])],"isStart":false});Q0=makeQuery(id+"F6.boolean.opBoolean","SPLIT",FACE,{"disambiguationData":[TD([makeQuery(id+"F6.opExtrude","SWEPT_FACE",FACE,{"disambiguationData":[OSD([sQuery(id+"F5.wireOp",EDGE,"E11")])]})])],"derivedFrom":makeQuery(id+"F4.opBoolean","MERGE",FACE,{"derivedFrom":[subQ0,makeQuery(id+"F3.opPattern","COPY",FACE,{"derivedFrom":subQ0,"instanceName":"1"}),makeQuery(id+"F3.opPattern","COPY",FACE,{"derivedFrom":subQ0,"instanceName":"2"}),makeQuery(id+"F3.opPattern","COPY",FACE,{"derivedFrom":subQ0,"instanceName":"3"}),makeQuery(id+"F3.opPattern","COPY",FACE,{"derivedFrom":subQ0,"instanceName":"4"}),makeQuery(id+"F3.opPattern","COPY",FACE,{"derivedFrom":subQ0,"instanceName":"5"}),makeQuery(id+"F3.opPattern","COPY",FACE,{"derivedFrom":subQ0,"instanceName":"6"}),makeQuery(id+"F3.opPattern","COPY",FACE,{"derivedFrom":subQ0,"instanceName":"7"}),makeQuery(id+"F3.opPattern","COPY",FACE,{"derivedFrom":subQ0,"instanceName":"8"}),makeQuery(id+"F3.opPattern","COPY",FACE,{"derivedFrom":subQ0,"instanceName":"9"}),makeQuery(id+"F3.opPattern","COPY",FACE,{"derivedFrom":subQ0,"instanceName":"10"}),makeQuery(id+"F3.opPattern","COPY",FACE,{"derivedFrom":subQ0,"instanceName":"11"}),makeQuery(id+"F3.opPattern","COPY",FACE,{"derivedFrom":subQ0,"instanceName":"12"}),makeQuery(id+"F3.opPattern","COPY",FACE,{"derivedFrom":subQ0,"instanceName":"13"}),makeQuery(id+"F3.opPattern","COPY",FACE,{"derivedFrom":subQ0,"instanceName":"14"}),makeQuery(id+"F3.opPattern","COPY",FACE,{"derivedFrom":subQ0,"instanceName":"15"}),makeQuery(id+"F3.opPattern","COPY",FACE,{"derivedFrom":subQ0,"instanceName":"16"}),makeQuery(id+"F3.opPattern","COPY",FACE,{"derivedFrom":subQ0,"instanceName":"17"}),makeQuery(id+"F3.opPattern","COPY",FACE,{"derivedFrom":subQ0,"instanceName":"18"}),makeQuery(id+"F3.opPattern","COPY",FACE,{"derivedFrom":subQ0,"instanceName":"19"}),makeQuery(id+"F3.opPattern","COPY",FACE,{"derivedFrom":subQ0,"instanceName":"20"}),makeQuery(id+"F3.opPattern","COPY",FACE,{"derivedFrom":subQ0,"instanceName":"21"}),makeQuery(id+"F3.opPattern","COPY",FACE,{"derivedFrom":subQ0,"instanceName":"22"}),makeQuery(id+"F3.opPattern","COPY",FACE,{"derivedFrom":subQ0,"instanceName":"23"}),makeQuery(id+"F3.opPattern","COPY",FACE,{"derivedFrom":subQ0,"instanceName":"24"}),makeQuery(id+"F3.opPattern","COPY",FACE,{"derivedFrom":subQ0,"instanceName":"25"}),makeQuery(id+"F3.opPattern","COPY",FACE,{"derivedFrom":subQ0,"instanceName":"26"}),makeQuery(id+"F3.opPattern","COPY",FACE,{"derivedFrom":subQ0,"instanceName":"27"}),makeQuery(id+"F3.opPattern","COPY",FACE,{"derivedFrom":subQ0,"instanceName":"28"}),makeQuery(id+"F3.opPattern","COPY",FACE,{"derivedFrom":subQ0,"instanceName":"29"}),makeQuery(id+"F3.opPattern","COPY",FACE,{"derivedFrom":subQ0,"instanceName":"30"}),makeQuery(id+"F3.opPattern","COPY",FACE,{"derivedFrom":subQ0,"instanceName":"31"}),makeQuery(id+"F3.opPattern","COPY",FACE,{"derivedFrom":subQ0,"instanceName":"32"}),makeQuery(id+"F3.opPattern","COPY",FACE,{"derivedFrom":subQ0,"instanceName":"33"}),makeQuery(id+"F3.opPattern","COPY",FACE,{"derivedFrom":subQ0,"instanceName":"34"}),makeQuery(id+"F3.opPattern","COPY",FACE,{"derivedFrom":subQ0,"instanceName":"35"}),makeQuery(id+"F3.opPattern","COPY",FACE,{"derivedFrom":subQ0,"instanceName":"36"}),makeQuery(id+"F3.opPattern","COPY",FACE,{"derivedFrom":subQ0,"instanceName":"37"}),makeQuery(id+"F3.opPattern","COPY",FACE,{"derivedFrom":subQ0,"instanceName":"38"}),makeQuery(id+"F3.opPattern","COPY",FACE,{"derivedFrom":subQ0,"instanceName":"39"}),makeQuery(id+"F3.opPattern","COPY",FACE,{"derivedFrom":subQ0,"instanceName":"40"}),makeQuery(id+"F3.opPattern","COPY",FACE,{"derivedFrom":subQ0,"instanceName":"41"}),makeQuery(id+"F3.opPattern","COPY",FACE,{"derivedFrom":subQ0,"instanceName":"42"}),makeQuery(id+"F3.opPattern","COPY",FACE,{"derivedFrom":subQ0,"instanceName":"43"}),makeQuery(id+"F3.opPattern","COPY",FACE,{"derivedFrom":subQ0,"instanceName":"44"}),makeQuery(id+"F3.opPattern","COPY",FACE,{"derivedFrom":subQ0,"instanceName":"45"}),makeQuery(id+"F3.opPattern","COPY",FACE,{"derivedFrom":subQ0,"instanceName":"46"}),makeQuery(id+"F3.opPattern","COPY",FACE,{"derivedFrom":subQ0,"instanceName":"47"}),makeQuery(id+"F3.opPattern","COPY",FACE,{"derivedFrom":subQ0,"instanceName":"48"}),makeQuery(id+"F3.opPattern","COPY",FACE,{"derivedFrom":subQ0,"instanceName":"49"}),makeQuery(id+"F3.opPattern","COPY",FACE,{"derivedFrom":subQ0,"instanceName":"50"}),makeQuery(id+"F3.opPattern","COPY",FACE,{"derivedFrom":subQ0,"instanceName":"51"}),makeQuery(id+"F3.opPattern","COPY",FACE,{"derivedFrom":subQ0,"instanceName":"52"}),makeQuery(id+"F3.opPattern","COPY",FACE,{"derivedFrom":subQ0,"instanceName":"53"}),makeQuery(id+"F3.opPattern","COPY",FACE,{"derivedFrom":subQ0,"instanceName":"54"}),makeQuery(id+"F3.opPattern","COPY",FACE,{"derivedFrom":subQ0,"instanceName":"55"}),makeQuery(id+"F3.opPattern","COPY",FACE,{"derivedFrom":subQ0,"instanceName":"56"}),makeQuery(id+"F3.opPattern","COPY",FACE,{"derivedFrom":subQ0,"instanceName":"57"}),makeQuery(id+"F3.opPattern","COPY",FACE,{"derivedFrom":subQ0,"instanceName":"58"}),makeQuery(id+"F3.opPattern","COPY",FACE,{"derivedFrom":subQ0,"instanceName":"59"})]})});}
            extrude(context, id + "F7", {"entities" : qUnion([Q0]), "operationType" : NewBodyOperationType.REMOVE, "oppositeDirection" : true, "depth" : 25.4 * mm, "offsetDistance" : 25.4 * mm});
        }
    });
